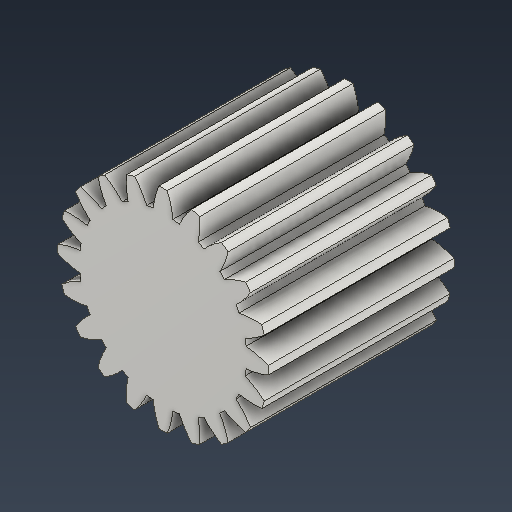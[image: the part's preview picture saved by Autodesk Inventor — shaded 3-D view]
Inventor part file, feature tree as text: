
AUTODESK INVENTOR PART (.ipt)
format: ipt  version: 2021 (Build 250183000, 183)  size: 274,432 bytes
history: native  units: mm (DEFAULTED — no unit token found)
features: plane x3, other x3, sketch x2, extrude x1
ambient origin geometry x8: Origin, YZ Plane, XZ Plane, XY Plane, X Axis, Y Axis, Z Axis, Center Point
bodies: Solid1 (feature_tree)
feature tree (9):
  extrude  "Extrusion1"  Depth=1.75mm TaperAngle=0.0deg
  plane  "Work Plane2"
  plane  "Work Plane8"
  plane  "Work Plane9"
  other  "Engrenagem reta"
  sketch  "Sketch1"  dims[d0=1.979988mm d1=1.75mm d2=0.0mm]
  sketch  "Sketch2"  dims[d3=1.8mm d4=10.0mm d5=0.0mm d16=3.597588mm d17=0.0mm d34=1.570796mm d39=0.0mm d41=0.0mm d43=3.597588mm d46=3.597588mm d47=0.0mm d48=0.0mm]
  other  "Srf1"
  other  "Diâmetro do flanco"
